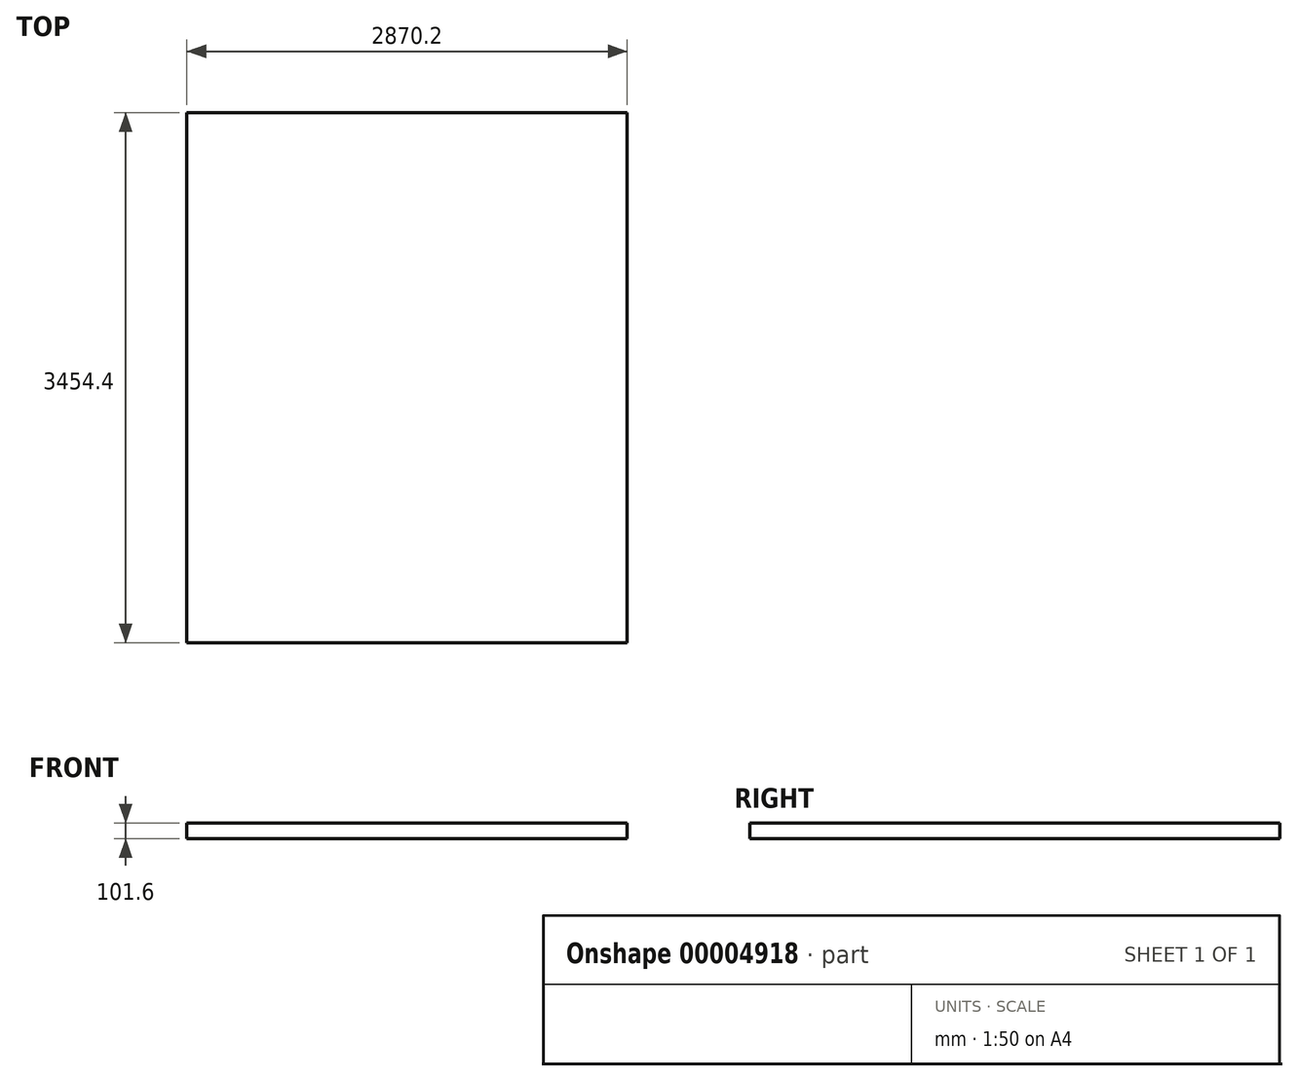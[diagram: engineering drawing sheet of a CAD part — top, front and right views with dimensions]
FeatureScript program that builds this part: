
annotation { "Feature Type Name" : "Feature", "Feature Type Description" : "" }
export const myFeature = defineFeature(function(context is Context, id is Id, definition is map)
    precondition{}
    {
        {
            var Q0;
            Q0=qCreatedBy(makeId("Top.planeOp"),FACE);
            var sketch = newSketch(context, id + "F0", { "sketchPlane" : qUnion([Q0])});
            skLineSegment(sketch, "E0.bottom", {"start": v(0, 0) * mm, "end": v(2870.2, 0) * mm});
            skLineSegment(sketch, "E0.top", {"start": v(0, 3454.4) * mm, "end": v(2870.2, 3454.4) * mm});
            skLineSegment(sketch, "E0.left", {"start": v(0, 0) * mm, "end": v(0, 3454.4) * mm});
            skLineSegment(sketch, "E0.right", {"start": v(2870.2, 0) * mm, "end": v(2870.2, 3454.4) * mm});
            skSolve(sketch);
        }
        {
            var Q0;
            Q0=qCreatedBy(makeId("Top.planeOp"),FACE);
            var sketch = newSketch(context, id + "F1", { "sketchPlane" : qUnion([Q0])});
            skLineSegment(sketch, "E1.bottom", {"start": v(0, 0) * mm, "end": v(2870.2, 0) * mm});
            skLineSegment(sketch, "E1.top", {"start": v(0, 3454.4) * mm, "end": v(2870.2, 3454.4) * mm});
            skLineSegment(sketch, "E1.left", {"start": v(0, 0) * mm, "end": v(0, 3454.4) * mm});
            skLineSegment(sketch, "E1.right", {"start": v(2870.2, 0) * mm, "end": v(2870.2, 3454.4) * mm});
            skSolve(sketch);
        }
        {
            var Q0;
            Q0=makeQuery(id+"F1.imprint","IMPRINT",FACE,{"disambiguationData":[TD([[makeQuery(id+"F1.imprint","IMPRINT",EDGE,{"derivedFrom":sQuery(id+"F1.wireOp",EDGE,"E1.bottom")}),1.0]])]});
            extrude(context, id + "F2", {"entities" : qUnion([Q0]), "depth" : 101.6 * mm});
        }
        {
            var Q0;
            Q0=makeQuery(id+"F2.opExtrude","CAP_FACE",FACE,{"disambiguationData":[OSD([sQuery(id+"F1.wireOp",EDGE,"E1.bottom"),sQuery(id+"F1.wireOp",EDGE,"E1.top"),sQuery(id+"F1.wireOp",EDGE,"E1.left"),sQuery(id+"F1.wireOp",EDGE,"E1.right")])],"isStart":false});
            var sketch = newSketch(context, id + "F3", { "sketchPlane" : qUnion([Q0])});
            skPoint(sketch, "E2", {"position": v(2717.8, 3302) * mm});
            skSolve(sketch);
        }
    });
